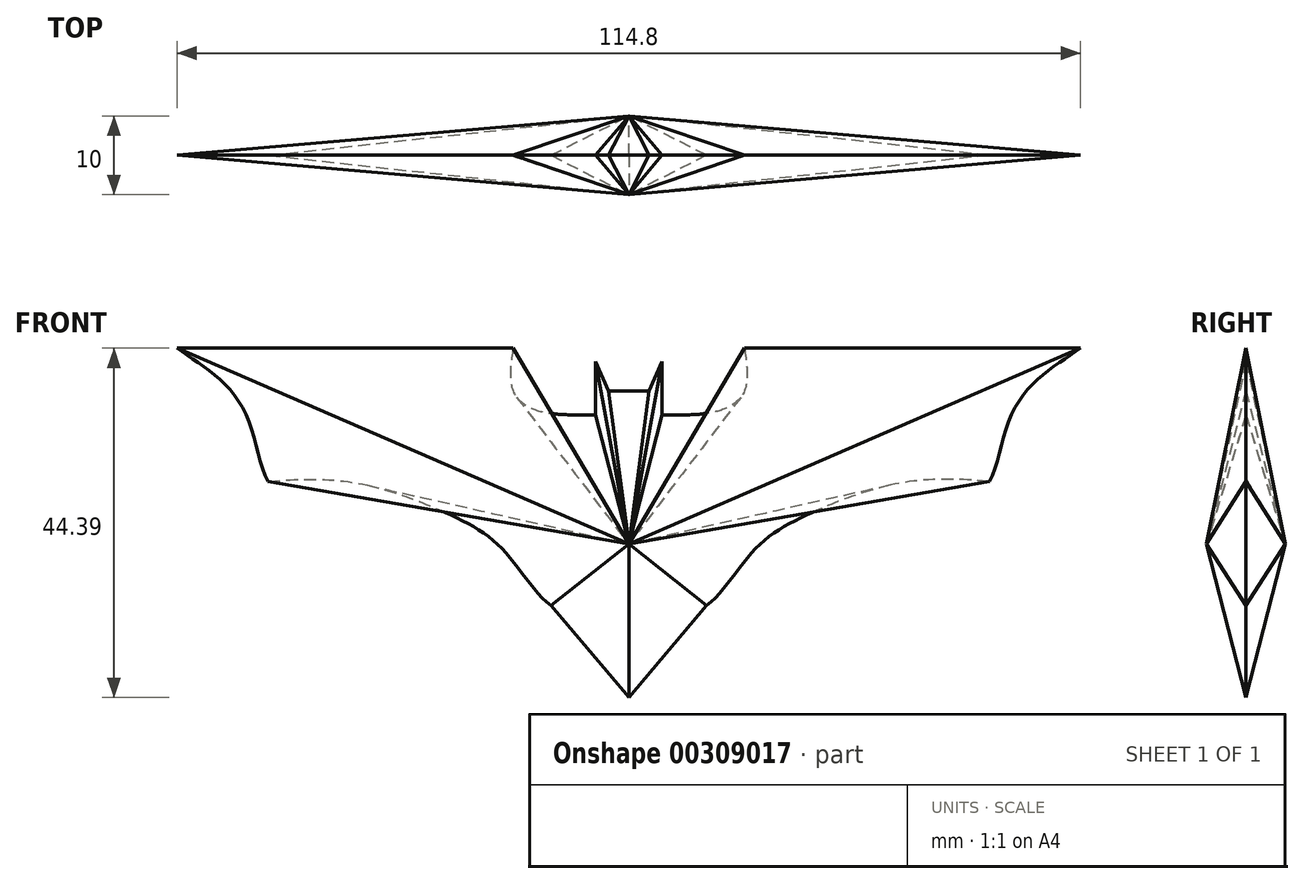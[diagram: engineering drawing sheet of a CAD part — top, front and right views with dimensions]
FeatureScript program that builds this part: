
annotation { "Feature Type Name" : "Feature", "Feature Type Description" : "" }
export const myFeature = defineFeature(function(context is Context, id is Id, definition is map)
    precondition{}
    {
        {
            var Q0;
            Q0=qCreatedBy(makeId("Front.planeOp"),FACE);
            var sketch = newSketch(context, id + "F0", { "sketchPlane" : qUnion([Q0])});
            skLineSegment(sketch, "E0", {"start": v(-64.61, 32.66) * mm, "end": v(-21.91, 32.66) * mm});
            skFitSpline(sketch, "E1", {"points": [v(-21.91, 32.66) * mm, v(-21.91, 27.24) * mm, v(-18.8, 24.74) * mm, v(-11.45, 24.18) * mm], "startDerivative": vector(-2.6, -17.95) * mm, "endDerivative": vector(20.75, 0.28) * mm});
            skFitSpline(sketch, "E2", {"points": [v(-64.61, 32.66) * mm, v(-59.8, 29.27) * mm, v(-55.56, 23.61) * mm, v(-53.02, 15.7) * mm], "startDerivative": vector(14.79, -10.4) * mm, "endDerivative": vector(9.6, -17.5) * mm});
            skLineSegment(sketch, "E3", {"start": v(-11.45, 24.18) * mm, "end": v(-11.45, 30.96) * mm});
            skLineSegment(sketch, "E4", {"start": v(-11.45, 30.96) * mm, "end": v(-9.76, 27.24) * mm});
            skLineSegment(sketch, "E5", {"start": v(-9.76, 27.24) * mm, "end": v(-7.21, 27.24) * mm});
            skFitSpline(sketch, "E6", {"points": [v(-53.02, 15.7) * mm, v(-42.84, 15.7) * mm, v(-30.4, 11.73) * mm, v(-23.05, 6.93) * mm, v(-17.1, 0) * mm], "startDerivative": vector(31.52, 3.1) * mm, "endDerivative": vector(28.21, -20.17) * mm});
            skLineSegment(sketch, "E7", {"start": v(-17.1, 0) * mm, "end": v(-7.21, -11.73) * mm});
            skLineSegment(sketch, "E8.MirrorCS", {"start": v(50.2, 32.66) * mm, "end": v(7.5, 32.66) * mm});
            skLineSegment(sketch, "E9.MirrorCS", {"start": v(-2.97, 24.18) * mm, "end": v(-2.97, 30.96) * mm});
            skLineSegment(sketch, "E10.MirrorCS", {"start": v(2.69, 0) * mm, "end": v(-7.21, -11.73) * mm});
            skFitSpline(sketch, "E11.MirrorCS", {"points": [v(38.6, 15.7) * mm, v(28.42, 15.7) * mm, v(15.98, 11.73) * mm, v(8.62, 6.93) * mm, v(2.69, 0) * mm], "startDerivative": vector(-31.52, 3.1) * mm, "endDerivative": vector(-28.21, -20.17) * mm});
            skFitSpline(sketch, "E12.MirrorCS", {"points": [v(50.2, 32.66) * mm, v(45.38, 29.27) * mm, v(41.14, 23.61) * mm, v(38.6, 15.7) * mm], "startDerivative": vector(-14.79, -10.4) * mm, "endDerivative": vector(-9.6, -17.5) * mm});
            skFitSpline(sketch, "E13.MirrorCS", {"points": [v(7.5, 32.66) * mm, v(7.5, 27.24) * mm, v(4.38, 24.74) * mm, v(-2.97, 24.18) * mm], "startDerivative": vector(2.6, -17.95) * mm, "endDerivative": vector(-20.75, 0.28) * mm});
            skLineSegment(sketch, "E14.MirrorCS", {"start": v(-2.97, 30.96) * mm, "end": v(-4.66, 27.24) * mm});
            skLineSegment(sketch, "E15.MirrorCS", {"start": v(-4.66, 27.24) * mm, "end": v(-7.21, 27.24) * mm});
            skPoint(sketch, "E16", {"position": v(-7.21, 7.75) * mm});
            skSolve(sketch);
        }
        {
            var Q0;
            Q0=qCreatedBy(makeId("Front.planeOp"),FACE);
            cPlane(context, id + "F1", {"entities" : qUnion([Q0]), "cplaneType" : CPlaneType.OFFSET, "offset" : 5 * mm, "width" : 150 * mm, "height" : 150 * mm});
        }
        {
            var Q0;
            Q0=qCreatedBy(id+"F1.planeOp",FACE);
            var sketch = newSketch(context, id + "F2", { "sketchPlane" : qUnion([Q0])});
            skPoint(sketch, "E17", {"position": v(-7.21, 7.78) * mm});
            skSolve(sketch);
        }
        {
            var Q0;
            Q0=makeQuery(id+"F0.imprint","IMPRINT",FACE,{"disambiguationData":[TD([[makeQuery(id+"F0.imprint","IMPRINT",EDGE,{"derivedFrom":sQuery(id+"F0.wireOp",EDGE,"E0")}),-1.0]])]});
            var Q1;
            Q1=sQuery(id+"F2.wireOp",VERTEX,"E17");
            loft(context, id + "F3", {"sheetProfilesArray" : [{ "sheetProfileEntities" : qUnion([Q0]) }, { "sheetProfileEntities" : qUnion([Q1]) }]});
        }
        {
            var Q0;
            Q0=qCreatedBy(makeId("Front.planeOp"),FACE);
            cPlane(context, id + "F4", {"entities" : qUnion([Q0]), "cplaneType" : CPlaneType.OFFSET, "offset" : 5 * mm, "oppositeDirection" : true, "width" : 150 * mm, "height" : 150 * mm});
        }
        {
            var Q0;
            Q0=qCreatedBy(id+"F4.planeOp",FACE);
            var sketch = newSketch(context, id + "F5", { "sketchPlane" : qUnion([Q0])});
            skPoint(sketch, "E18", {"position": v(-7.21, 7.78) * mm});
            skSolve(sketch);
        }
        {
            var Q1;
            Q1=makeQuery(id+"F0.imprint","IMPRINT",FACE,{"disambiguationData":[TD([[makeQuery(id+"F0.imprint","IMPRINT",EDGE,{"derivedFrom":sQuery(id+"F0.wireOp",EDGE,"E0")}),-1.0]])]});
            var Q2;
            Q2=sQuery(id+"F5.wireOp",VERTEX,"E18");
            loft(context, id + "F6", {"operationType" : NewBodyOperationType.ADD, "sheetProfilesArray" : [{ "sheetProfileEntities" : qUnion([Q1]) }, { "sheetProfileEntities" : qUnion([Q2]) }]});
        }
    });
